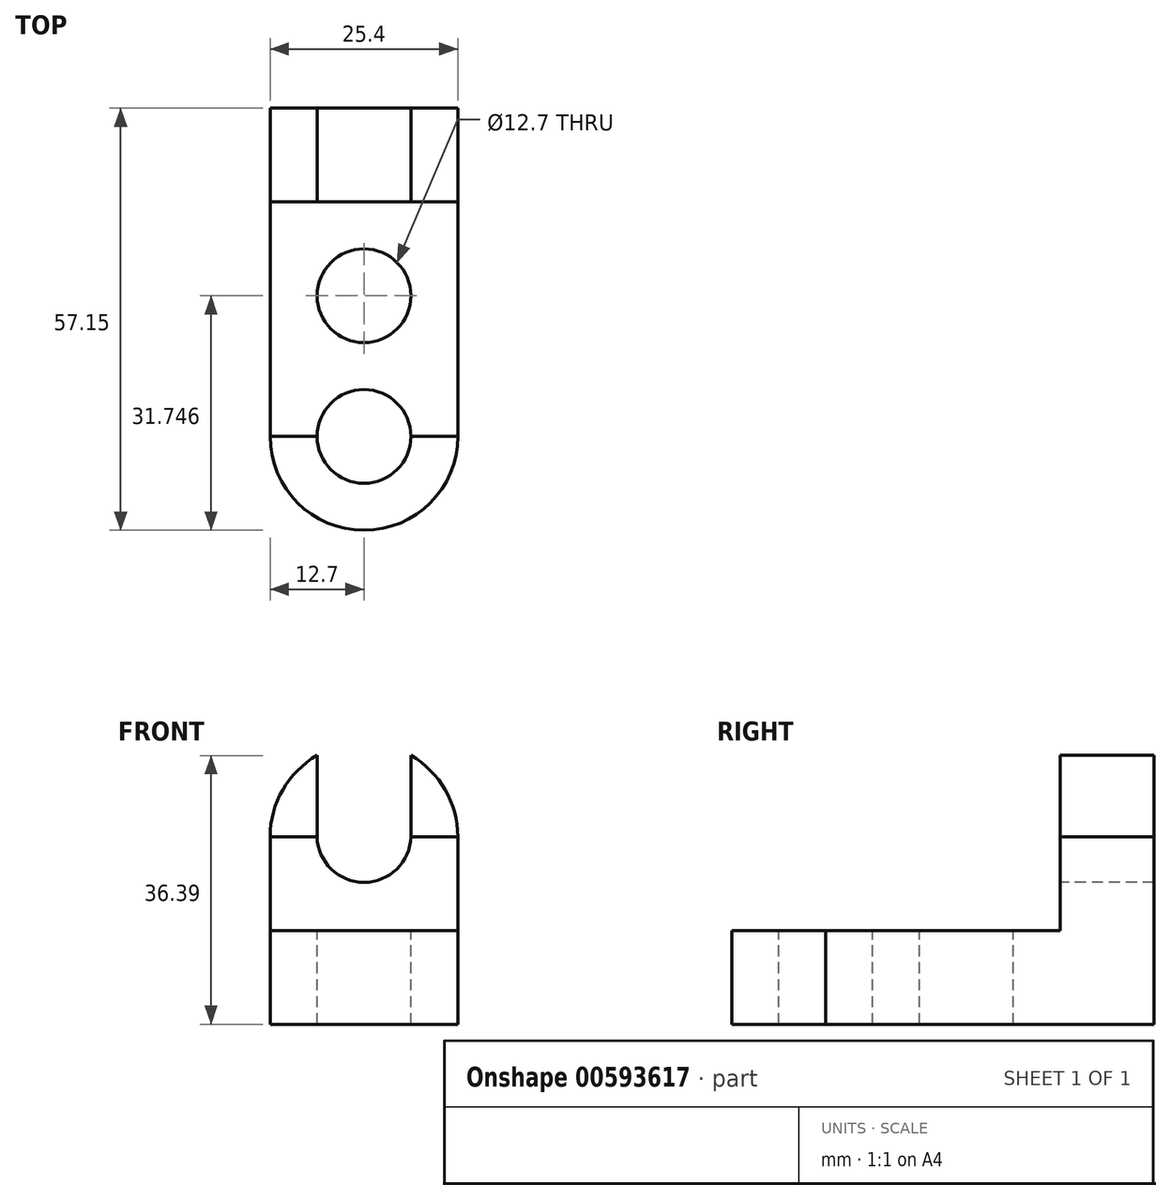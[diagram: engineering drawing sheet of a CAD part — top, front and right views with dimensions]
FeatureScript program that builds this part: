
annotation { "Feature Type Name" : "Feature", "Feature Type Description" : "" }
export const myFeature = defineFeature(function(context is Context, id is Id, definition is map)
    precondition{}
    {
        {
            var Q0;
            Q0=qCreatedBy(makeId("Right.planeOp"),FACE);
            var sketch = newSketch(context, id + "F0", { "sketchPlane" : qUnion([Q0])});
            skLineSegment(sketch, "E0", {"start": v(62.03, 58.04) * mm, "end": v(62.03, 32.64) * mm});
            skLineSegment(sketch, "E1", {"start": v(62.03, 32.64) * mm, "end": v(17.58, 32.64) * mm});
            skLineSegment(sketch, "E2", {"start": v(17.58, 32.64) * mm, "end": v(17.58, 45.34) * mm});
            skLineSegment(sketch, "E3", {"start": v(17.58, 45.34) * mm, "end": v(49.33, 45.34) * mm});
            skLineSegment(sketch, "E4", {"start": v(49.33, 45.34) * mm, "end": v(49.33, 58.04) * mm});
            skLineSegment(sketch, "E5", {"start": v(49.33, 58.04) * mm, "end": v(62.03, 58.04) * mm});
            skSolve(sketch);
        }
        {
            var Q0;
            Q0 = qSketchRegion(id + "F0", true);
            extrude(context, id + "F1", {"entities" : qUnion([Q0]), "depth" : 25.4 * mm, "offsetDistance" : 25.4 * mm});
        }
        {
            var Q0;
            Q0=makeQuery(id+"F1.opExtrude","SWEPT_FACE",FACE,{"disambiguationData":[OSD([sQuery(id+"F0.wireOp",EDGE,"E3")])]});
            var sketch = newSketch(context, id + "F2", { "sketchPlane" : qUnion([Q0])});
            skArc(sketch, "E6", {"start": v(0, 17.58) * mm, "mid": v(12.7, 4.88) * mm, "end": v(25.4, 17.58) * mm});
            skLineSegment(sketch, "E7", {"start": v(25.4, 17.58) * mm, "end": v(0, 17.58) * mm});
            skSolve(sketch);
        }
        {
            var Q0;
            Q0 = qSketchRegion(id + "F2", true);
            extrude(context, id + "F3", {"entities" : qUnion([Q0]), "oppositeDirection" : true, "depth" : 12.7 * mm, "offsetDistance" : 25.4 * mm});
        }
        {
            var Q0;
            Q0=makeQuery(id+"F1.opExtrude","SWEPT_FACE",FACE,{"disambiguationData":[OSD([sQuery(id+"F0.wireOp",EDGE,"E3")])]});
            var sketch = newSketch(context, id + "F4", { "sketchPlane" : qUnion([Q0])});
            skCircle(sketch, "E8", {"center": v(12.7, 36.63) * mm, "radius": 6.35 * mm});
            skCircle(sketch, "E9", {"center": v(12.7, 17.58) * mm, "radius": 6.35 * mm});
            skSolve(sketch);
        }
        {
            var Q0;
            Q0=makeQuery(id+"F4.imprint","IMPRINT",FACE,{"disambiguationData":[TD([[makeQuery(id+"F4.imprint","IMPRINT",EDGE,{"derivedFrom":sQuery(id+"F4.wireOp",EDGE,"E8")}),1.0]])]});
            var Q1;
            {var subQ0=sQuery(id+"F4.wireOp",EDGE,"E9");var subQ1=makeQuery(id+"F1.opExtrude","SWEPT_EDGE",EDGE,{"disambiguationData":[OSD([sQuery(id+"F0.wireOp",EDGE,"E2"),sQuery(id+"F0.wireOp",EDGE,"E3")])]});var subQ2=makeQuery(id+"F4.imprint","INTERSECT",VERTEX,{"disambiguationData":[OD(0.0)],"derivedFrom":[subQ1,subQ0]});Q1=makeQuery(id+"F4.imprint","IMPRINT",FACE,{"disambiguationData":[TD([[makeQuery(id+"F4.imprint","IMPRINT",EDGE,{"disambiguationData":[TD([[subQ2,1.0]])],"derivedFrom":subQ0}),1.0]])]});}
            extrude(context, id + "F5", {"entities" : qUnion([Q0, Q1]), "operationType" : NewBodyOperationType.REMOVE, "oppositeDirection" : true, "depth" : 12.7 * mm, "offsetDistance" : 25.4 * mm});
        }
        {
            var Q0;
            Q0=makeQuery(id+"F3.opExtrude","CAP_FACE",FACE,{"disambiguationData":[OSD([sQuery(id+"F2.wireOp",EDGE,"E6"),sQuery(id+"F2.wireOp",EDGE,"E7")])],"isStart":true});
            var sketch = newSketch(context, id + "F6", { "sketchPlane" : qUnion([Q0])});
            skCircle(sketch, "E10", {"center": v(12.7, 17.58) * mm, "radius": 6.35 * mm});
            skSolve(sketch);
        }
        {
            var Q0;
            {var subQ0=sQuery(id+"F6.wireOp",EDGE,"E10");var subQ1=makeQuery(id+"F3.opExtrude","CAP_EDGE",EDGE,{"disambiguationData":[OSD([sQuery(id+"F2.wireOp",EDGE,"E7")])],"isStart":true});var subQ2=makeQuery(id+"F6.imprint","INTERSECT",VERTEX,{"disambiguationData":[OD(0.0)],"derivedFrom":[subQ1,subQ0]});Q0=makeQuery(id+"F6.imprint","IMPRINT",FACE,{"disambiguationData":[TD([[makeQuery(id+"F6.imprint","IMPRINT",EDGE,{"disambiguationData":[TD([[subQ2,-1.0]])],"derivedFrom":subQ0}),1.0]])]});}
            extrude(context, id + "F7", {"entities" : qUnion([Q0]), "operationType" : NewBodyOperationType.REMOVE, "oppositeDirection" : true, "depth" : 12.7 * mm, "offsetDistance" : 25.4 * mm});
        }
        {
            var Q0;
            Q0=makeQuery(id+"F1.opExtrude","SWEPT_FACE",FACE,{"disambiguationData":[OSD([sQuery(id+"F0.wireOp",EDGE,"E4")])]});
            var sketch = newSketch(context, id + "F8", { "sketchPlane" : qUnion([Q0])});
            skArc(sketch, "E11", {"start": v(6.35, 58.04) * mm, "mid": v(12.7, 51.85) * mm, "end": v(19.05, 58.04) * mm});
            skLineSegment(sketch, "E12", {"start": v(6.35, 58.04) * mm, "end": v(19.05, 58.04) * mm});
            skSolve(sketch);
        }
        {
            var Q0;
            Q0 = qSketchRegion(id + "F8", true);
            extrude(context, id + "F9", {"entities" : qUnion([Q0]), "operationType" : NewBodyOperationType.REMOVE, "oppositeDirection" : true, "depth" : 12.7 * mm, "offsetDistance" : 25.4 * mm});
        }
        {
            var Q0;
            Q0=qCreatedBy(makeId("Front.planeOp"),FACE);
            var sketch = newSketch(context, id + "F10", { "sketchPlane" : qUnion([Q0])});
            skLineSegment(sketch, "E13", {"start": v(6.35, 57.98) * mm, "end": v(6.35, 64.33) * mm});
            skLineSegment(sketch, "E14", {"start": v(6.35, 64.33) * mm, "end": v(19.05, 64.33) * mm});
            skLineSegment(sketch, "E15", {"start": v(19.05, 64.33) * mm, "end": v(19.05, 57.98) * mm});
            skLineSegment(sketch, "E16", {"start": v(19.05, 57.98) * mm, "end": v(6.35, 57.98) * mm});
            skSolve(sketch);
        }
        {
            var Q0;
            Q0 = qSketchRegion(id + "F10", true);
            extrude(context, id + "F11", {"entities" : qUnion([Q0]), "operationType" : NewBodyOperationType.REMOVE, "oppositeDirection" : true, "depth" : 12.7 * mm, "offsetDistance" : 25.4 * mm});
        }
        {
            var Q0;
            Q0=qCreatedBy(makeId("Front.planeOp"),FACE);
            var sketch = newSketch(context, id + "F12", { "sketchPlane" : qUnion([Q0])});
            skLineSegment(sketch, "E17", {"start": v(6.35, 58.29) * mm, "end": v(6.35, 64.64) * mm});
            skLineSegment(sketch, "E18", {"start": v(6.35, 64.64) * mm, "end": v(19.05, 64.64) * mm});
            skLineSegment(sketch, "E19", {"start": v(19.05, 64.64) * mm, "end": v(19.05, 58.29) * mm});
            skLineSegment(sketch, "E20", {"start": v(19.05, 58.29) * mm, "end": v(6.35, 58.29) * mm});
            skSolve(sketch);
        }
        {
            var Q0;
            Q0 = qSketchRegion(id + "F12", true);
            extrude(context, id + "F13", {"entities" : qUnion([Q0]), "operationType" : NewBodyOperationType.REMOVE, "oppositeDirection" : true, "depth" : 12.7 * mm, "offsetDistance" : 25.4 * mm});
        }
        {
            var Q0;
            Q0=makeQuery(id+"F1.opExtrude","SWEPT_FACE",FACE,{"disambiguationData":[OSD([sQuery(id+"F0.wireOp",EDGE,"E4")])]});
            var sketch = newSketch(context, id + "F14", { "sketchPlane" : qUnion([Q0])});
            skArc(sketch, "E21", {"start": v(25.4, 58.04) * mm, "mid": v(12.7, 70.74) * mm, "end": v(0, 58.04) * mm});
            skLineSegment(sketch, "E22", {"start": v(0, 58.04) * mm, "end": v(25.4, 58.04) * mm});
            skSolve(sketch);
        }
        {
            var Q0;
            Q0 = qSketchRegion(id + "F14", true);
            extrude(context, id + "F15", {"entities" : qUnion([Q0]), "oppositeDirection" : true, "depth" : 12.7 * mm, "offsetDistance" : 25.4 * mm});
        }
        {
            var Q0;
            Q0=makeQuery(id+"F15.opExtrude","CAP_FACE",FACE,{"disambiguationData":[OSD([sQuery(id+"F14.wireOp",EDGE,"E21"),sQuery(id+"F14.wireOp",EDGE,"E22")])],"isStart":true});
            var sketch = newSketch(context, id + "F16", { "sketchPlane" : qUnion([Q0])});
            skLineSegment(sketch, "E23", {"start": v(6.35, 58.04) * mm, "end": v(6.35, 72.92) * mm});
            skLineSegment(sketch, "E24", {"start": v(6.35, 72.92) * mm, "end": v(19.05, 72.92) * mm});
            skLineSegment(sketch, "E25", {"start": v(19.05, 72.92) * mm, "end": v(19.05, 58.04) * mm});
            skLineSegment(sketch, "E26", {"start": v(19.05, 58.04) * mm, "end": v(6.35, 58.04) * mm});
            skSolve(sketch);
        }
        {
            var Q0;
            Q0 = qSketchRegion(id + "F16", true);
            extrude(context, id + "F17", {"entities" : qUnion([Q0]), "operationType" : NewBodyOperationType.REMOVE, "oppositeDirection" : true, "depth" : 12.7 * mm, "offsetDistance" : 25.4 * mm});
        }
    });
